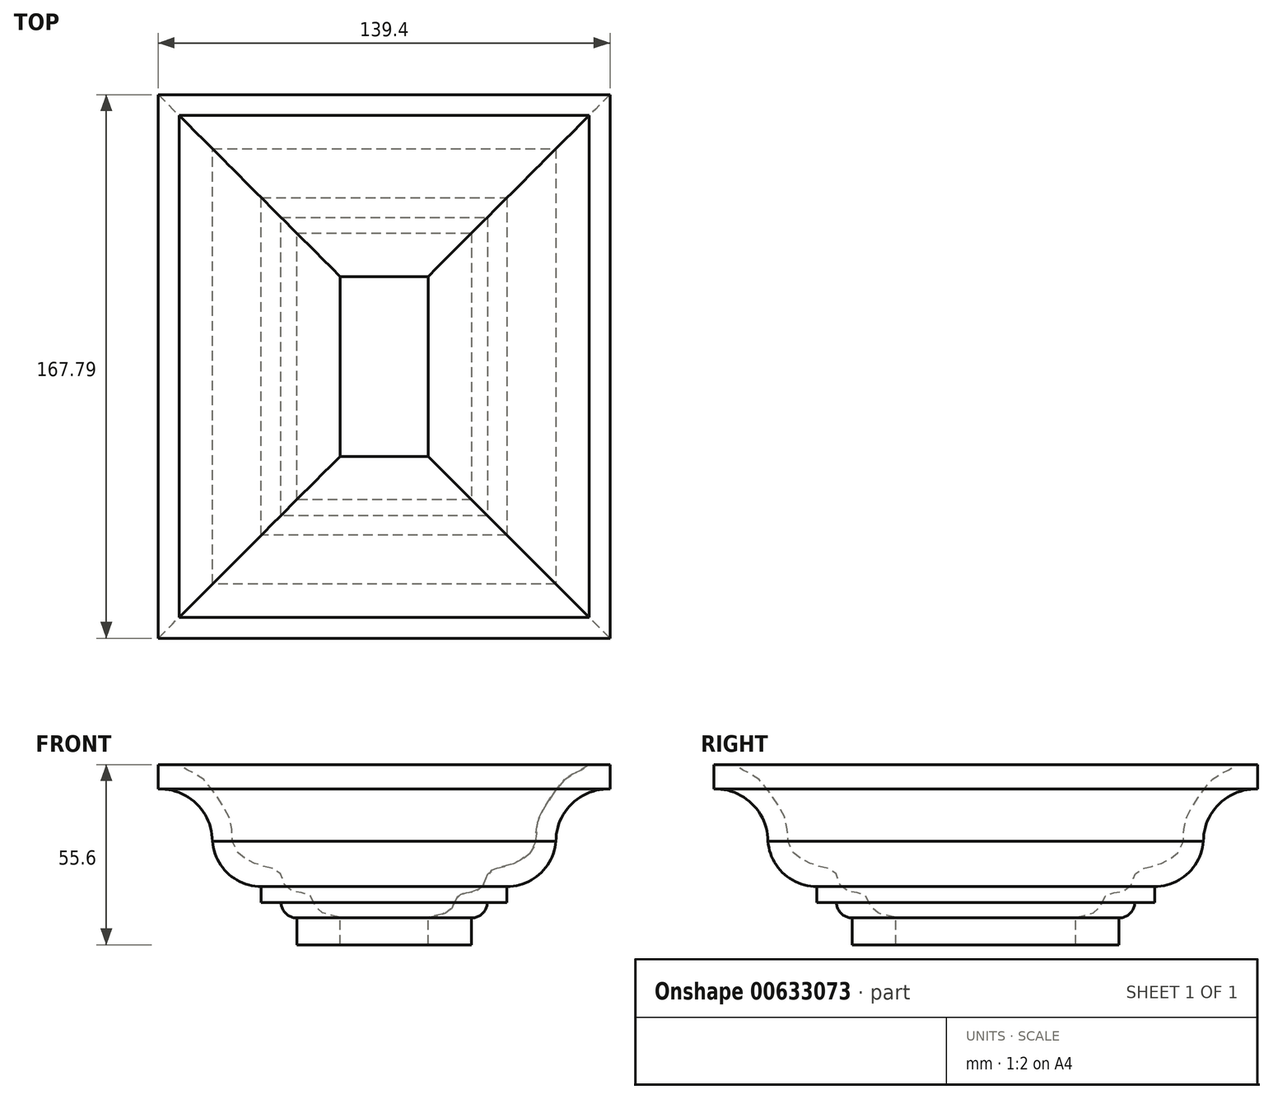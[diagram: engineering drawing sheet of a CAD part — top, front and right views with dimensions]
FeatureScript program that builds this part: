
annotation { "Feature Type Name" : "Feature", "Feature Type Description" : "" }
export const myFeature = defineFeature(function(context is Context, id is Id, definition is map)
    precondition{}
    {
        {
            var Q0;
            Q0=qCreatedBy(makeId("Front.planeOp"),FACE);
            var sketch = newSketch(context, id + "F0", { "sketchPlane" : qUnion([Q0])});
            skLineSegment(sketch, "E0", {"start": v(0, 0) * mm, "end": v(13.4, 0) * mm});
            skLineSegment(sketch, "E1", {"start": v(13.4, 0) * mm, "end": v(13.4, 8.28) * mm});
            skArc(sketch, "E2", {"start": v(13.4, 8.28) * mm, "mid": v(16.8, 9.67) * mm, "end": v(18.27, 13.06) * mm});
            skLineSegment(sketch, "E3", {"start": v(18.27, 13.06) * mm, "end": v(24.35, 13.06) * mm});
            skLineSegment(sketch, "E4", {"start": v(24.35, 13.06) * mm, "end": v(24.35, 17.98) * mm});
            skArc(sketch, "E5", {"start": v(24.35, 17.98) * mm, "mid": v(34.62, 22) * mm, "end": v(39.42, 31.94) * mm});
            skArc(sketch, "E6", {"start": v(39.42, 31.94) * mm, "mid": v(44.35, 43.57) * mm, "end": v(56.13, 48.1) * mm});
            skLineSegment(sketch, "E7", {"start": v(56.13, 48.1) * mm, "end": v(56.13, 55.6) * mm});
            skLineSegment(sketch, "E8", {"start": v(56.13, 55.6) * mm, "end": v(49.7, 55.6) * mm});
            skLineSegment(sketch, "E9", {"start": v(0, 0) * mm, "end": v(0, 8.51) * mm});
            skFitSpline(sketch, "E10", {"points": [v(49.7, 55.6) * mm, v(46.52, 53.58) * mm, v(42.8, 51.59) * mm, v(40.82, 49.47) * mm, v(38.17, 46.02) * mm, v(34.85, 40.59) * mm, v(33.53, 36.74) * mm, v(33, 30.91) * mm, v(30.35, 27.33) * mm, v(25.18, 24.68) * mm, v(21.2, 23.62) * mm, v(18.15, 21.5) * mm, v(16.3, 17.26) * mm, v(10.6, 15.8) * mm, v(8.08, 13.42) * mm, v(7.02, 10.77) * mm, v(0, 8.51) * mm], "startDerivative": vector(-52.52, -36.65) * mm, "endDerivative": vector(-110.7, -20.05) * mm});
            skSolve(sketch);
        }
        {
            var Q0;
            Q0=qCreatedBy(makeId("Top.planeOp"),FACE);
            var sketch = newSketch(context, id + "F1", { "sketchPlane" : qUnion([Q0])});
            skLineSegment(sketch, "E11", {"start": v(13.34, 11.67) * mm, "end": v(13.34, -28.72) * mm});
            skLineSegment(sketch, "E12", {"start": v(13.34, -28.72) * mm, "end": v(-40.48, -28.72) * mm});
            skLineSegment(sketch, "E13", {"start": v(-40.48, -28.72) * mm, "end": v(-40.48, 53.49) * mm});
            skLineSegment(sketch, "E14", {"start": v(-40.48, 53.49) * mm, "end": v(13.34, 53.49) * mm});
            skLineSegment(sketch, "E15", {"start": v(13.34, 53.49) * mm, "end": v(13.34, 11.67) * mm});
            skSolve(sketch);
        }
        {
            var Q0;
            Q0=makeQuery(id+"F0.imprint","IMPRINT",FACE,{"disambiguationData":[TD([[makeQuery(id+"F0.imprint","IMPRINT",EDGE,{"derivedFrom":sQuery(id+"F0.wireOp",EDGE,"E0")}),1.0]])]});
            var Q1;
            Q1=sQuery(id+"F1.wireOp",EDGE,"E12");
            var Q2;
            Q2=sQuery(id+"F1.wireOp",EDGE,"E11");
            var Q3;
            Q3=sQuery(id+"F1.wireOp",EDGE,"E13");
            var Q4;
            Q4=sQuery(id+"F1.wireOp",EDGE,"E14");
            var Q5;
            Q5=sQuery(id+"F1.wireOp",EDGE,"E15");
            sweep(context, id + "F2", {"profiles" : qUnion([Q0]), "path" : qUnion([Q1, Q2, Q3, Q4, Q5])});
        }
    });
